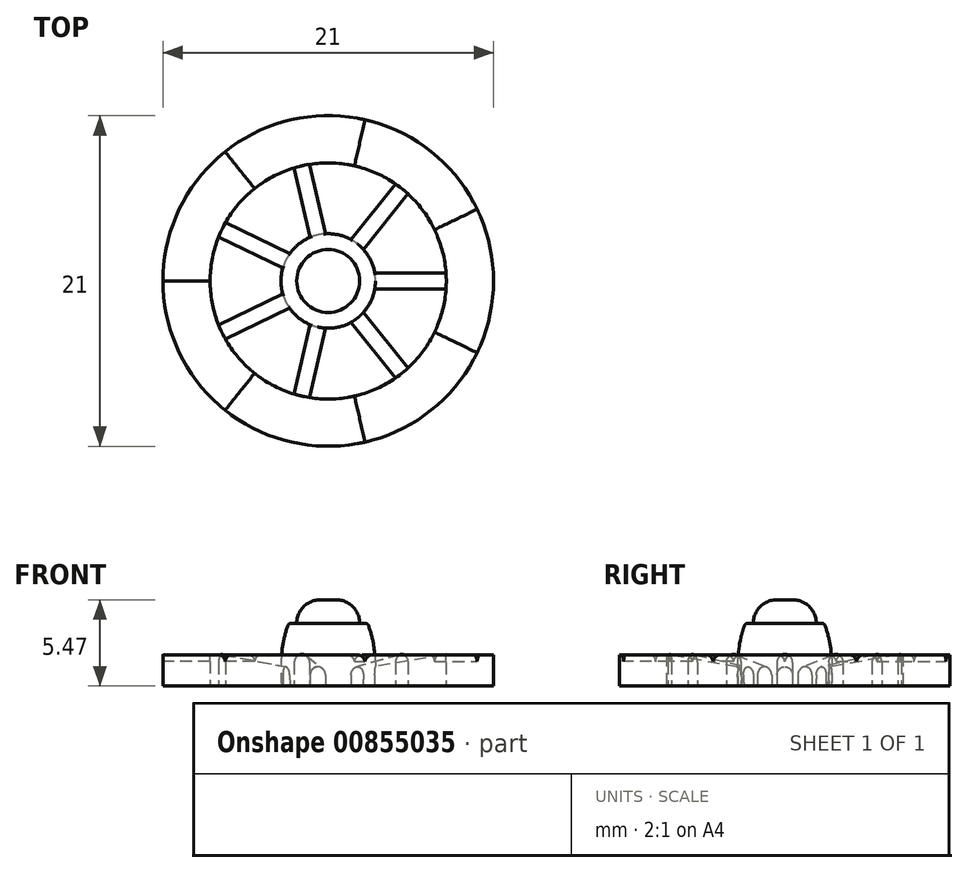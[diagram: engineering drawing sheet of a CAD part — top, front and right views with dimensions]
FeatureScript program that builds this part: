
annotation { "Feature Type Name" : "Feature", "Feature Type Description" : "" }
export const myFeature = defineFeature(function(context is Context, id is Id, definition is map)
    precondition{}
    {
        {
            var Q0;
            Q0=qCreatedBy(makeId("Front.planeOp"),FACE);
            var sketch = newSketch(context, id + "F0", { "sketchPlane" : qUnion([Q0])});
            skLineSegment(sketch, "E0", {"start": v(0, 3) * mm, "end": v(2.5, 3) * mm});
            skLineSegment(sketch, "E1", {"start": v(0, -3) * mm, "end": v(2.5, -3) * mm});
            skFitSpline(sketch, "E2", {"points": [v(2.5, 3) * mm, v(3, 0) * mm, v(2.5, -3) * mm], "startDerivative": vector(2.5, -6) * mm, "endDerivative": vector(-2.5, -6) * mm});
            skLineSegment(sketch, "E3", {"start": v(0, 3) * mm, "end": v(0, -3) * mm});
            skSolve(sketch);
        }
        {
            var Q0;
            Q0=makeQuery(id+"F0.imprint","IMPRINT",FACE,{"disambiguationData":[TD([[makeQuery(id+"F0.imprint","IMPRINT",EDGE,{"derivedFrom":sQuery(id+"F0.wireOp",EDGE,"E0")}),-1.0]])]});
            var Q1;
            Q1=sQuery(id+"F0.wireOp",EDGE,"E3");
            revolve(context, id + "F1", {"surfaceOperationType" : NewSurfaceOperationType.NEW, "entities" : qUnion([Q0]), "axis" : qUnion([Q1]), "revolveType" : RevolveType.SYMMETRIC, "angle" : 51.5 * degree});
        }
        {
            var Q0;
            Q0=qCreatedBy(makeId("Front.planeOp"),FACE);
            var sketch = newSketch(context, id + "F2", { "sketchPlane" : qUnion([Q0])});
            skLineSegment(sketch, "E4", {"start": v(7.5, -0.97) * mm, "end": v(10.5, -0.97) * mm});
            skLineSegment(sketch, "E5", {"start": v(10.5, -0.97) * mm, "end": v(10.5, 1.03) * mm});
            skLineSegment(sketch, "E6", {"start": v(10.5, 1.03) * mm, "end": v(7.5, 1.03) * mm});
            skLineSegment(sketch, "E7", {"start": v(7.5, 1.03) * mm, "end": v(1.59, 0) * mm});
            skPoint(sketch, "E8.0", {"position": v(2.5, -3) * mm});
            skFitSpline(sketch, "E9.0", {"points": [v(2.5, 3) * mm, v(2.92, 2) * mm, v(3.08, 0) * mm, v(2.92, -2) * mm, v(2.5, -3) * mm]});
            skLineSegment(sketch, "E10", {"start": v(7.5, 1.03) * mm, "end": v(7.5, -0.97) * mm});
            skLineSegment(sketch, "E11", {"start": v(1.59, 0) * mm, "end": v(1.59, -0.97) * mm});
            skLineSegment(sketch, "E12", {"start": v(1.59, -0.97) * mm, "end": v(7.5, -0.97) * mm});
            skSolve(sketch);
        }
        {
            var Q0;
            {var subQ0=sQuery(id+"F2.wireOp",EDGE,"E10");Q0=makeQuery(id+"F2.imprint","IMPRINT",FACE,{"disambiguationData":[TD([[makeQuery(id+"F2.imprint","IMPRINT",EDGE,{"derivedFrom":subQ0}),-1.0]])]});}
            var Q1;
            {var subQ0=sQuery(id+"F2.wireOp",EDGE,"E11");Q1=makeQuery(id+"F2.imprint","IMPRINT",FACE,{"disambiguationData":[TD([[makeQuery(id+"F2.imprint","IMPRINT",EDGE,{"derivedFrom":subQ0}),1.0]])]});}
            extrude(context, id + "F3", {"entities" : qUnion([Q0, Q1]), "operationType" : NewBodyOperationType.ADD, "endBound" : BoundingType.SYMMETRIC, "depth" : 1 * mm, "offsetDistance" : 25 * mm});
        }
        {
            var Q0;
            Q0=qCreatedBy(makeId("Top.planeOp"),FACE);
            var sketch = newSketch(context, id + "F4", { "sketchPlane" : qUnion([Q0])});
            skPoint(sketch, "E13.0", {"position": v(7.5, 0) * mm});
            skCircle(sketch, "E14", {"center": v(0, 0) * mm, "radius": 7.5 * mm});
            skCircle(sketch, "E15", {"center": v(0, 0) * mm, "radius": 10.5 * mm});
            skLineSegment(sketch, "E16", {"start": v(0, 0) * mm, "end": v(9.46, 4.56) * mm});
            skLineSegment(sketch, "E17", {"start": v(0, 0) * mm, "end": v(9.46, -4.56) * mm});
            skLineSegment(sketch, "E18", {"start": v(7.5, 0) * mm, "end": v(9.46, 4.56) * mm, "construction": true});
            skLineSegment(sketch, "E19", {"start": v(7.5, 0) * mm, "end": v(9.46, -4.56) * mm, "construction": true});
            skSolve(sketch);
        }
        {
            var Q0;
            {var subQ0=sQuery(id+"F4.wireOp",EDGE,"E16");var subQ1=sQuery(id+"F4.wireOp",EDGE,"E14");var subQ2=makeQuery(id+"F4.imprint","INTERSECT",VERTEX,{"derivedFrom":[subQ1,subQ0]});Q0=makeQuery(id+"F4.imprint","IMPRINT",FACE,{"disambiguationData":[TD([[makeQuery(id+"F4.imprint","IMPRINT",EDGE,{"disambiguationData":[TD([[subQ2,1.0]])],"derivedFrom":subQ1}),-1.0]])]});}
            var Q1;
            Q1=makeQuery(id+"F3.opExtrude","SWEPT_FACE",FACE,{"disambiguationData":[OSD([sQuery(id+"F2.wireOp",EDGE,"E12")])]});
            extrude(context, id + "F5", {"entities" : qUnion([Q0]), "operationType" : NewBodyOperationType.ADD, "depth" : 1 * mm, "offsetDistance" : 25 * mm, "hasSecondDirection" : true, "secondDirectionBound" : SecondDirectionBoundingType.UP_TO_SURFACE, "secondDirectionOppositeDirection" : true, "secondDirectionDepth" : 25 * mm, "secondDirectionBoundEntityFace" : qUnion([Q1])});
        }
        {
            var Q0;
            Q0=makeQuery(id+"F5.opExtrude","CAP_EDGE",EDGE,{"disambiguationData":[OSD([sQuery(id+"F4.wireOp",EDGE,"E17")])],"isStart":false});
            var Q1;
            Q1=makeQuery(id+"F5.opExtrude","CAP_EDGE",EDGE,{"disambiguationData":[OSD([sQuery(id+"F4.wireOp",EDGE,"E16")])],"isStart":false});
            fillet(context, id + "F6", {"entities" : qUnion([Q0, Q1]), "radius" : .5 * mm, "tangentPropagation" : true, "allowEdgeOverflow" : false});
        }
        {
            var Q0;
            Q0=makeQuery(id+"F1.opRevolve","SWEPT_EDGE",EDGE,{"disambiguationData":[OSD([sQuery(id+"F0.wireOp",EDGE,"E0"),sQuery(id+"F0.wireOp",EDGE,"E2")])]});
            var Q1;
            Q1=makeQuery(id+"F1.opRevolve","SWEPT_EDGE",EDGE,{"disambiguationData":[OSD([sQuery(id+"F0.wireOp",EDGE,"E1"),sQuery(id+"F0.wireOp",EDGE,"E2")])]});
            fillet(context, id + "F7", {"entities" : qUnion([Q0, Q1]), "radius" : .2 * mm, "tangentPropagation" : true, "allowEdgeOverflow" : false});
        }
        {
            var Q0;
            Q0=makeQuery(id+"F3.opExtrude","CAP_EDGE",EDGE,{"disambiguationData":[OSD([sQuery(id+"F2.wireOp",EDGE,"E7")])],"isStart":true});
            var Q1;
            Q1=makeQuery(id+"F3.opExtrude","CAP_EDGE",EDGE,{"disambiguationData":[OSD([sQuery(id+"F2.wireOp",EDGE,"E7")])],"isStart":false});
            fillet(context, id + "F8", {"entities" : qUnion([Q0, Q1]), "radius" : .5 * mm, "tangentPropagation" : true, "allowEdgeOverflow" : false});
        }
        {
            var Q0;
            Q0=makeQuery(id+"F3.opExtrude","SWEPT_BODY",BODY,{"disambiguationData":[OSD([sQuery(id+"F2.wireOp",EDGE,"P3XRHdqQ-L2r8-D6yd-624t-mKVHREpRhMzi"),sQuery(id+"F2.wireOp",EDGE,"E7"),sQuery(id+"F2.wireOp",EDGE,"E9.0"),sQuery(id+"F2.wireOp",EDGE,"E10")])]});
            var Q1;
            Q1=makeQuery(id+"F1.opRevolve","SWEPT_BODY",BODY,{"disambiguationData":[OSD([sQuery(id+"F0.wireOp",EDGE,"E0"),sQuery(id+"F0.wireOp",EDGE,"E1"),sQuery(id+"F0.wireOp",EDGE,"E2"),sQuery(id+"F0.wireOp",EDGE,"E3")])]});
            var Q2;
            Q2=sQuery(id+"F0.wireOp",EDGE,"E3");
            circularPattern(context, id + "F9", {"operationType" : NewBodyOperationType.ADD, "entities" : qUnion([Q0, Q1]), "axis" : qUnion([Q2]), "angle" : 360 * degree, "instanceCount" : 7, "equalSpace" : true});
        }
        {
            var Q0;
            Q0=makeQuery(id+"F1.opRevolve","SWEPT_FACE",FACE,{"disambiguationData":[OSD([sQuery(id+"F0.wireOp",EDGE,"E0")])]});
            var sketch = newSketch(context, id + "F10", { "sketchPlane" : qUnion([Q0])});
            skCircle(sketch, "E20", {"center": v(0, 0) * mm, "radius": 2 * mm});
            skSolve(sketch);
        }
        {
            var Q0;
            Q0=makeQuery(id+"F10.imprint","IMPRINT",FACE,{"disambiguationData":[TD([[makeQuery(id+"F10.imprint","IMPRINT",EDGE,{"derivedFrom":sQuery(id+"F10.wireOp",EDGE,"E20")}),1.0]])]});
            extrude(context, id + "F11", {"entities" : qUnion([Q0]), "operationType" : NewBodyOperationType.ADD, "depth" : 1.5 * mm, "offsetDistance" : 25 * mm});
        }
        {
            var Q0;
            Q0=makeQuery(id+"F11.opExtrude","CAP_EDGE",EDGE,{"disambiguationData":[OSD([sQuery(id+"Fo0OBk3eU98LPMd_1.wireOp",EDGE,"aklb42WT-bPkk-FSHh-G9pr-mXH5jjUrZlTj")])],"isStart":false});
            var Q1;
            Q1=makeQuery(id+"F11.opExtrude","CAP_EDGE",EDGE,{"disambiguationData":[OSD([sQuery(id+"F10.wireOp",EDGE,"E20")])],"isStart":false});
            fillet(context, id + "F12", {"entities" : qUnion([Q0, Q1]), "radius" : 1.5 * mm, "tangentPropagation" : true, "allowEdgeOverflow" : false});
        }
        {
            var Q0;
            Q0=makeQuery(id+"F1.opRevolve","SWEPT_FACE",FACE,{"disambiguationData":[OSD([sQuery(id+"F0.wireOp",EDGE,"E1")])]});
            var sketch = newSketch(context, id + "F13", { "sketchPlane" : qUnion([Q0])});
            skCircle(sketch, "E21", {"center": v(0, 0) * mm, "radius": 1 * mm});
            skSolve(sketch);
        }
        {
            var Q0;
            {var subQ0=makeQuery(id+"F1.opRevolve","SWEPT_FACE",FACE,{"disambiguationData":[OSD([sQuery(id+"F0.wireOp",EDGE,"E1")])]});Q0=makeQuery(id+"F9.boolean.opBoolean","MERGE",FACE,{"derivedFrom":[subQ0,makeQuery(id+"F9.opPattern","COPY",FACE,{"derivedFrom":subQ0,"instanceName":"1"}),makeQuery(id+"F9.opPattern","COPY",FACE,{"derivedFrom":subQ0,"instanceName":"2"}),makeQuery(id+"F9.opPattern","COPY",FACE,{"derivedFrom":subQ0,"instanceName":"3"}),makeQuery(id+"F9.opPattern","COPY",FACE,{"derivedFrom":subQ0,"instanceName":"4"}),makeQuery(id+"F9.opPattern","COPY",FACE,{"derivedFrom":subQ0,"instanceName":"5"}),makeQuery(id+"F9.opPattern","COPY",FACE,{"derivedFrom":subQ0,"instanceName":"6"})]});}
            var sketch = newSketch(context, id + "F14", { "sketchPlane" : qUnion([Q0])});
            skCircle(sketch, "E22", {"center": v(0, 0) * mm, "radius": 3.5 * mm});
            skSolve(sketch);
        }
        {
            var Q0;
            Q0=makeQuery(id+"F14.imprint","IMPRINT",FACE,{"disambiguationData":[TD([[makeQuery(id+"F14.imprint","IMPRINT",EDGE,{"derivedFrom":sQuery(id+"F14.wireOp",EDGE,"E22")}),1.0]])]});
            var Q1;
            Q1=makeQuery(id+"F14.imprint","IMPRINT",FACE,{"disambiguationData":[TD([[makeQuery(id+"F14.imprint","IMPRINT",EDGE,{"derivedFrom":makeQuery(id+"FyldBqjJfOwkMDB_1.boolean.opBoolean","COPY",EDGE,{"derivedFrom":makeQuery(id+"FyldBqjJfOwkMDB_1.opExtrude","CAP_EDGE",EDGE,{"disambiguationData":[OSD([sQuery(id+"F13.wireOp",EDGE,"E21")])],"isStart":true})})}),-1.0]])]});
            var Q2;
            Q2=makeQuery(id+"F13.imprint","IMPRINT",FACE,{"disambiguationData":[TD([[makeQuery(id+"F13.imprint","IMPRINT",EDGE,{"derivedFrom":sQuery(id+"F13.wireOp",EDGE,"E21")}),1.0]])]});
            var Q3;
            Q3=makeQuery(id+"F13.imprint","IMPRINT",FACE,{"disambiguationData":[TD([[makeQuery(id+"F13.imprint","IMPRINT",EDGE,{"derivedFrom":sQuery(id+"F13.wireOp",EDGE,"E21")}),-1.0]])]});
            var Q4;
            {var subQ0=sQuery(id+"F2.wireOp",EDGE,"E12");var subQ1=makeQuery(id+"FhDZsmcsc9Nekxo_1.opExtrude","CAP_FACE",FACE,{"disambiguationData":[OSD([subQ0])],"isStart":false});var subQ2=makeQuery(id+"F5.boolean.opBoolean","MERGE",FACE,{"derivedFrom":[makeQuery(id+"F3.opExtrude","SWEPT_FACE",FACE,{"disambiguationData":[OSD([subQ0])]}),makeQuery(id+"F5.opExtrude","CAP_FACE",FACE,{"disambiguationData":[OSD([subQ0])],"isStart":true})]});Q4=makeQuery(id+"F5OMLmibTjMQsVw_2.boolean.opBoolean","MERGE",FACE,{"derivedFrom":[makeQuery(id+"F9.boolean.opBoolean","MERGE",FACE,{"derivedFrom":[subQ2,makeQuery(id+"F9.opPattern","COPY",FACE,{"derivedFrom":subQ2,"instanceName":"1"}),makeQuery(id+"F9.opPattern","COPY",FACE,{"derivedFrom":subQ2,"instanceName":"2"}),makeQuery(id+"F9.opPattern","COPY",FACE,{"derivedFrom":subQ2,"instanceName":"3"}),makeQuery(id+"F9.opPattern","COPY",FACE,{"derivedFrom":subQ2,"instanceName":"4"}),makeQuery(id+"F9.opPattern","COPY",FACE,{"derivedFrom":subQ2,"instanceName":"5"}),makeQuery(id+"F9.opPattern","COPY",FACE,{"derivedFrom":subQ2,"instanceName":"6"})]}),subQ1,makeQuery(id+"F5OMLmibTjMQsVw_2.opPattern","COPY",FACE,{"derivedFrom":subQ1,"instanceName":"1"}),makeQuery(id+"F5OMLmibTjMQsVw_2.opPattern","COPY",FACE,{"derivedFrom":subQ1,"instanceName":"2"}),makeQuery(id+"F5OMLmibTjMQsVw_2.opPattern","COPY",FACE,{"derivedFrom":subQ1,"instanceName":"3"}),makeQuery(id+"F5OMLmibTjMQsVw_2.opPattern","COPY",FACE,{"derivedFrom":subQ1,"instanceName":"4"}),makeQuery(id+"F5OMLmibTjMQsVw_2.opPattern","COPY",FACE,{"derivedFrom":subQ1,"instanceName":"5"}),makeQuery(id+"F5OMLmibTjMQsVw_2.opPattern","COPY",FACE,{"derivedFrom":subQ1,"instanceName":"6"})]});}
            extrude(context, id + "F15", {"entities" : qUnion([Q0, Q1, Q2, Q3]), "operationType" : NewBodyOperationType.REMOVE, "endBound" : BoundingType.UP_TO_SURFACE, "oppositeDirection" : true, "depth" : 25 * mm, "endBoundEntityFace" : qUnion([Q4]), "offsetDistance" : 25 * mm});
        }
    });
